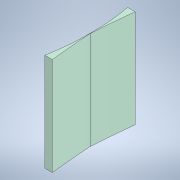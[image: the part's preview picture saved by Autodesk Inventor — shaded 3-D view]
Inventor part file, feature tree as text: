
AUTODESK INVENTOR PART (.ipt)
format: ipt  version: 2021 (Build 250183000, 183)  size: 117,760 bytes
history: native  units: mm
features: extrude x1, sketch x1
ambient origin geometry x8: Origin, YZ Plane, XZ Plane, XY Plane, X Axis, Y Axis, Z Axis, Center Point
bodies: Solid1 (feature_tree)
feature tree (2):
  extrude  "Extrusion1"  Depth=200.0mm
  sketch  "Sketch1"  dims[d0=85.0mm d1=14.835299mm d2=430.0mm d3=85.0mm d4=14.835299mm d5=430.0mm d6=85.0mm d7=16.580628mm d10=85.0mm d11=16.580628mm d12=200.0mm d13=0.0mm]
